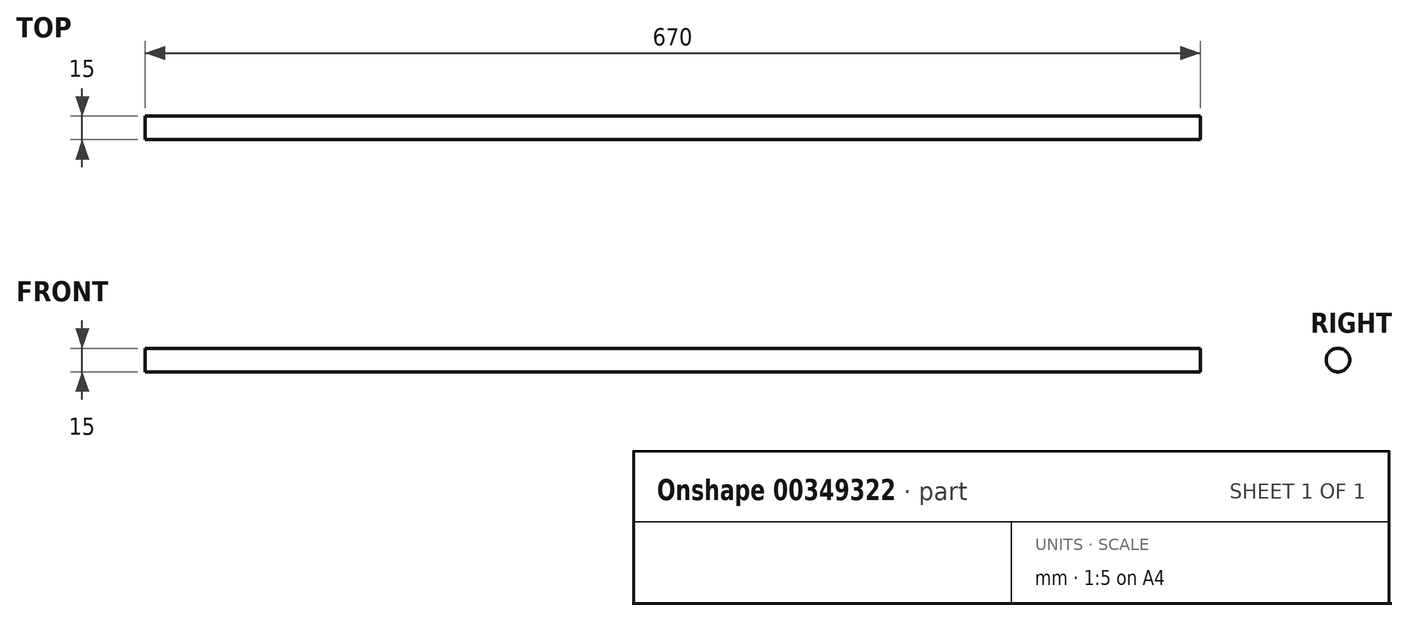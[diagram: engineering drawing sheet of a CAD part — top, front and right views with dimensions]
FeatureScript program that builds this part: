
annotation { "Feature Type Name" : "Feature", "Feature Type Description" : "" }
export const myFeature = defineFeature(function(context is Context, id is Id, definition is map)
    precondition{}
    {
        {
            var Q0;
            Q0=qCreatedBy(makeId("Front.planeOp"),FACE);
            var sketch = newSketch(context, id + "F0", { "sketchPlane" : qUnion([Q0])});
            skLineSegment(sketch, "E0.bottom", {"start": v(335, 7.5) * mm, "end": v(-335, 7.5) * mm});
            skLineSegment(sketch, "E0.top", {"start": v(335, -7.5) * mm, "end": v(-335, -7.5) * mm});
            skLineSegment(sketch, "E0.left", {"start": v(335, 7.5) * mm, "end": v(335, -7.5) * mm});
            skLineSegment(sketch, "E0.right", {"start": v(-335, 7.5) * mm, "end": v(-335, -7.5) * mm});
            skPoint(sketch, "E0.middle", {"position": v(0, 0) * mm});
            skSolve(sketch);
        }
        {
            var Q0;
            Q0 = qSketchRegion(id + "F0", true);
            extrude(context, id + "F1", {"entities" : qUnion([Q0]), "endBound" : BoundingType.SYMMETRIC, "depth" : 15 * mm});
        }
        {
            var Q0;
            Q0=makeQuery(id+"F1.opExtrude","CAP_EDGE",EDGE,{"disambiguationData":[OSD([sQuery(id+"F0.wireOp",EDGE,"E0.top")])],"isStart":true});
            var Q1;
            Q1=makeQuery(id+"F1.opExtrude","CAP_EDGE",EDGE,{"disambiguationData":[OSD([sQuery(id+"F0.wireOp",EDGE,"E0.top")])],"isStart":false});
            var Q2;
            Q2=makeQuery(id+"F1.opExtrude","CAP_EDGE",EDGE,{"disambiguationData":[OSD([sQuery(id+"F0.wireOp",EDGE,"E0.bottom")])],"isStart":false});
            var Q3;
            Q3=makeQuery(id+"F1.opExtrude","CAP_EDGE",EDGE,{"disambiguationData":[OSD([sQuery(id+"F0.wireOp",EDGE,"E0.bottom")])],"isStart":true});
            fillet(context, id + "F2", {"entities" : qUnion([Q0, Q1, Q2, Q3]), "radius" : 7.5 * mm, "tangentPropagation" : true, "allowEdgeOverflow" : false});
        }
    });
